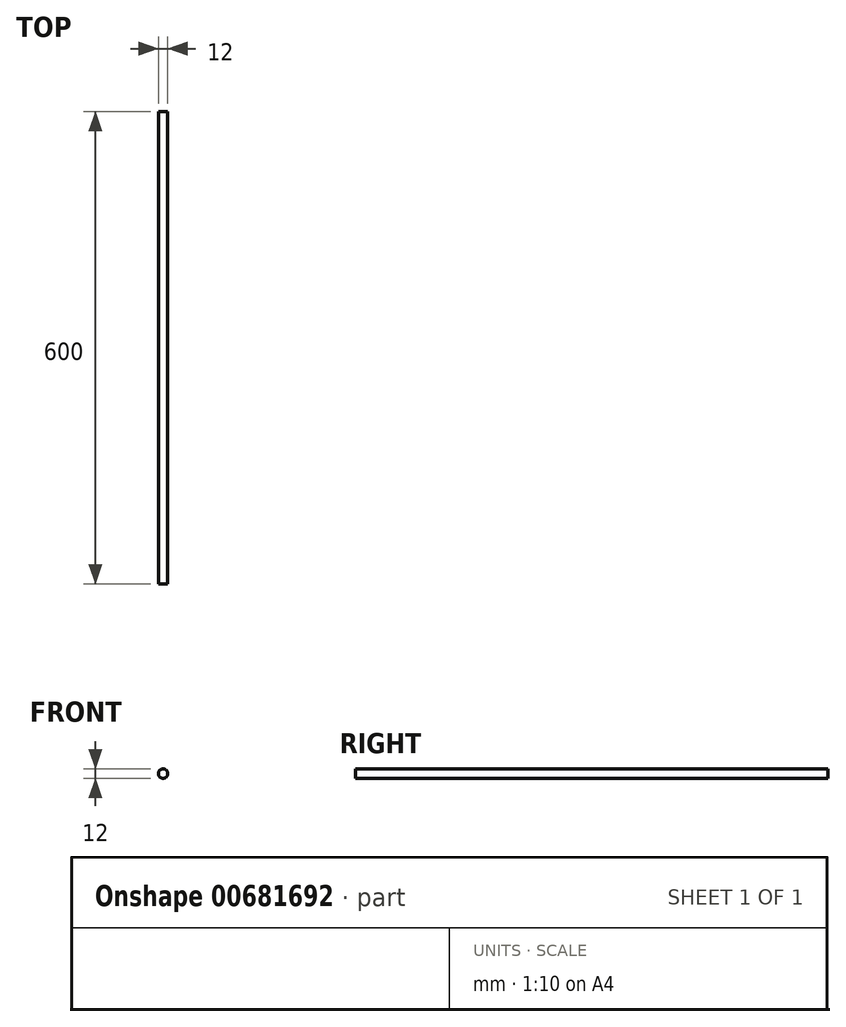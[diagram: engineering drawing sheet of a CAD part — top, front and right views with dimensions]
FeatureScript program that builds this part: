
annotation { "Feature Type Name" : "Feature", "Feature Type Description" : "" }
export const myFeature = defineFeature(function(context is Context, id is Id, definition is map)
    precondition{}
    {
        {
            var Q0;
            Q0=qCreatedBy(makeId("Front.planeOp"),FACE);
            var sketch = newSketch(context, id + "F0", { "sketchPlane" : qUnion([Q0])});
            skCircle(sketch, "E0", {"center": v(0, 0) * mm, "radius": 6 * mm});
            skSolve(sketch);
        }
        {
            var Q0;
            Q0 = qSketchRegion(id + "F0", true);
            extrude(context, id + "F1", {"entities" : qUnion([Q0]), "depth" : 600 * mm, "offsetDistance" : 25 * mm});
        }
    });
